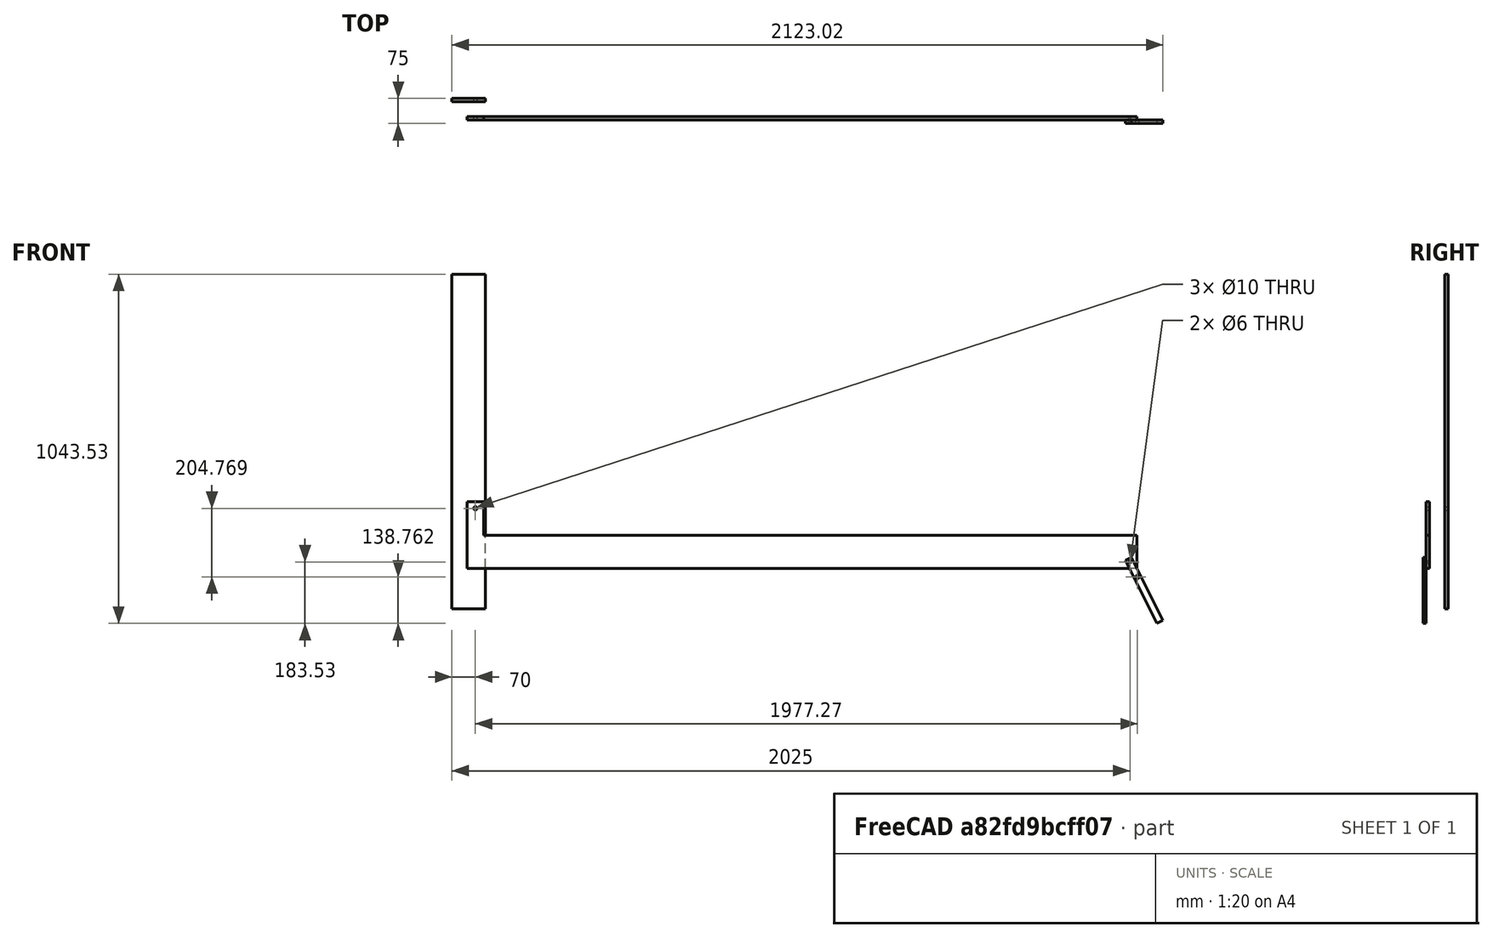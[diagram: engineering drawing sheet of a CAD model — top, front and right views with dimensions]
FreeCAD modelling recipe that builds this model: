
FCSTD DOCUMENT  (FreeCAD 2022.524R14555 (Git shallow))
Label: assembly
License: All rights reserved
LicenseURL: http://en.wikipedia.org/wiki/All_rights_reserved
objects: Part::FeaturePython×17, App::FeaturePython×13, Sketcher::SketchObject×5, PartDesign::Body×4, PartDesign::Pad×3, PartDesign::Hole×3, Part::SubShapeBinder×2, PartDesign::SubShapeBinder×1
note: 46 computed .brp shape members not serialized (recipe doc carries the construction recipe); baked Part::Feature solids carry a one-line shape summary decoded from their .brp

FEATURE [Sketcher::SketchObject] Sketch
  FullyConstrained = true
  MapMode = 5
  Placement = pos=(0,0,0) rot=(1,0,0;1.5708rad)
  Support = -> [XZ_Plane]
  TreeRank = 27
  sketch-geometry (5):
    g0: LineSegment StartX=0 StartY=0 StartZ=0 EndX=100 EndY=0 EndZ=0
    g1: LineSegment StartX=100 StartY=0 StartZ=0 EndX=100 EndY=1000 EndZ=0
    g2: LineSegment StartX=100 StartY=1000 StartZ=0 EndX=0 EndY=1000 EndZ=0
    g3: LineSegment StartX=0 StartY=1000 StartZ=0 EndX=0 EndY=0 EndZ=0
    g4: Circle CenterX=70 CenterY=300 CenterZ=0 NormalX=0 NormalY=0 NormalZ=1 AngleXU=0 Radius=5
  constraints (14):
    c: Coincident(g0,g1)
    c: Coincident(g1,g2)
    c: Coincident(g2,g3)
    c: Coincident(g3,g0)
    c: Horizontal(g0)
    c: Horizontal(g2)
    c: Vertical(g1)
    c: Vertical(g3)
    c: Coincident(g0,g-1)
    c: Distance(g0) = 100
    c: Distance(g1) = 1000
    c: Diameter(g4) = 10
    c: DistanceY(g0,g4) = 300
    c: DistanceX(g4,g0) = 30
FEATURE [PartDesign::Pad] Pad
  AddSubType = 0
  AlongSketchNormal = false
  CheckUpToFaceLimits = true
  ClaimChildren = false
  Direction = (0,-1,2e-16)
  Fit = 0
  FitJoin = 0
  InnerFit = 0
  InnerFitJoin = 0
  InnerTaperAngle = 0
  InnerTaperAngleRev = 0
  Length = 10
  Length2 = 100
  Linearize = true
  NewSolid = false
  Placement = pos=(0,0,0) rot=(1,0,0;1.5708rad)
  Profile = -> Sketch
  Suppress = false
  TreeRank = 28
  Type = 0
  _ProfileBasedVersion = 1
FEATURE [Sketcher::SketchObject] Sketch001
  FullyConstrained = false
  MapMode = 5
  Placement = pos=(1.13238e+06,-2.32641e+06,1.04291e+07) rot=(0.99859,0.005814,-0.052765;3.36076rad)
  TreeRank = 42
  sketch-geometry (7):
    g0: LineSegment StartX=2173.24 StartY=237.393 StartZ=0 EndX=2173.24 EndY=137.393 EndZ=0
    g1: LineSegment StartX=2173.24 StartY=137.393 StartZ=0 EndX=173.238 EndY=137.393 EndZ=0
    g2: LineSegment StartX=173.238 StartY=137.393 StartZ=0 EndX=173.238 EndY=337.393 EndZ=0
    g3: LineSegment StartX=173.238 StartY=337.393 StartZ=0 EndX=223.238 EndY=337.393 EndZ=0
    g4: LineSegment StartX=223.238 StartY=337.393 StartZ=0 EndX=223.238 EndY=237.393 EndZ=0
    g5: LineSegment StartX=223.238 StartY=237.393 StartZ=0 EndX=2173.24 EndY=237.393 EndZ=0
    g6: Circle CenterX=198.238 CenterY=317.393 CenterZ=0 NormalX=0 NormalY=0 NormalZ=1 AngleXU=0 Radius=5
  constraints (19):
    c: Coincident(g0,g1)
    c: Coincident(g1,g2)
    c: Horizontal(g1)
    c: Vertical(g0)
    c: Vertical(g2)
    c: Coincident(g2,g3)
    c: Horizontal(g3)
    c: Coincident(g3,g4)
    c: Vertical(g4)
    c: Coincident(g4,g5)
    c: Coincident(g5,g0)
    c: Horizontal(g5)
    c: Distance(g1) = 2000
    c: Distance(g0) = 100
    c: Distance(g4) = 100
    c: Distance(g3) = 50
    c: DistanceX(g6,g3) = 25
    c: Diameter(g6) = 10
    c: DistanceY(g6,g2) = 20
FEATURE [PartDesign::Pad] Pad001
  AddSubType = 0
  AlongSketchNormal = false
  CheckUpToFaceLimits = true
  ClaimChildren = false
  Direction = (-0.105384,0.216506,-0.970577)
  Fit = 0
  FitJoin = 0
  InnerFit = 0
  InnerFitJoin = 0
  InnerTaperAngle = 0
  InnerTaperAngleRev = 0
  Length = 10
  Length2 = 100
  Linearize = true
  NewSolid = false
  Placement = pos=(1.13238e+06,-2.32641e+06,1.04291e+07) rot=(0.99859,0.005814,-0.052765;3.36076rad)
  Profile = -> Sketch001
  Suppress = false
  TreeRank = 44
  Type = 0
  _ProfileBasedVersion = 1
FEATURE [Sketcher::SketchObject] Sketch002
  ExternalGeometry = -> [Pad001]
  FullyConstrained = true
  MapMode = 5
  Placement = pos=(1.13238e+06,-2.32641e+06,1.04291e+07) rot=(0.99859,0.005814,-0.052765;3.36076rad)
  Support = -> [Pad001]
  TreeRank = 90
  sketch-geometry (1):
    g0: Circle CenterX=2153.24 CenterY=157.393 CenterZ=0 NormalX=0 NormalY=0 NormalZ=1 AngleXU=0 Radius=5
  constraints (3):
    c: DistanceY(g-3,g0) = 20
    c: DistanceX(g0,g-3) = 20
    c: Diameter(g0) = 10
FEATURE [PartDesign::Hole] Hole
  AddSubType = 1
  BaseFeature = -> Pad001
  ClaimChildren = false
  CustomThreadClearance = 0
  Depth = 25
  DepthType = 0
  Diameter = 6
  DrillForDepth = false
  DrillPoint = 1
  DrillPointAngle = 118
  Fit = 0
  FitJoin = 0
  HoleCutCountersinkAngle = 90
  HoleCutCustomValues = false
  HoleCutDepth = 0
  HoleCutDiameter = 6.1
  HoleCutType = 0
  InnerFit = 0
  InnerFitJoin = 0
  Linearize = true
  ModelThread = false
  NewSolid = false
  Placement = pos=(1.13238e+06,-2.32641e+06,1.04291e+07) rot=(0.99859,0.005814,-0.052765;3.36076rad)
  Profile = -> Sketch002
  Suppress = false
  Tapered = false
  TaperedAngle = 90
  ThreadClass = 0
  ThreadDepth = 23.5
  ThreadDepthType = 0
  ThreadDirection = 0
  ThreadFit = 0
  ThreadSize = 0
  ThreadType = 0
  Threaded = false
  TreeRank = 91
  UseCustomThreadClearance = false
  _ProfileBasedVersion = 1
FEATURE [PartDesign::Body] Body001  label="Ramme"
  AutoGroupSolids = false
  ClaimAllChildren = false
  ExportMode = 0
  Group = -> [Sketch001,Pad001,Sketch002,Hole]
  Origin = -> Origin001
  Placement = pos=(-128.238,-1.07453e+07,-17.3929) rot=(-0.997715,-0.052719,0.042254;1.79251rad)
  Tip = -> Hole
  TreeRank = 41
  _ExportChildren = -> [Pad001,Hole]
  _GroupVersion = 1
FEATURE [Part::SubShapeBinder] Import  label="Import(Hole)"
  BindCopyOnChange = 0
  BindMode = 0
  ClaimChildren = false
  Context = -> Assembly [Parts.Body002.Import.]
  FillStyle = 0
  Fuse = false
  MakeFace = false
  PartialLoad = false
  Relative = true
  Support = -> [Body001[Hole.]]
  TreeRank = 103
  _Version = 8
FEATURE [Sketcher::SketchObject] Sketch003
  ExternalGeometry = -> [Import]
  FullyConstrained = true
  MapMode = 5
  Placement = pos=(8.58341,-49.4299,-44.7434) rot=(0.99755,0.02837,0.063948;2.30829rad)
  Support = -> [Import]
  TreeRank = 102
  sketch-geometry (6):
    g0: LineSegment StartX=1907.59 StartY=351.564 StartZ=0 EndX=1927.59 EndY=351.564 EndZ=0
    g1: LineSegment StartX=1927.59 StartY=351.564 StartZ=0 EndX=1927.59 EndY=141.564 EndZ=0
    g2: LineSegment StartX=1927.59 StartY=141.564 StartZ=0 EndX=1907.59 EndY=141.564 EndZ=0
    g3: LineSegment StartX=1907.59 StartY=141.564 StartZ=0 EndX=1907.59 EndY=351.564 EndZ=0
    g4: Circle CenterX=1917.59 CenterY=341.564 CenterZ=0 NormalX=0 NormalY=0 NormalZ=1 AngleXU=0 Radius=3
    g5: Circle CenterX=1917.59 CenterY=291.564 CenterZ=0 NormalX=0 NormalY=0 NormalZ=1 AngleXU=0 Radius=5
  constraints (17):
    c: Coincident(g0,g1)
    c: Coincident(g1,g2)
    c: Coincident(g2,g3)
    c: Horizontal(g0)
    c: Horizontal(g2)
    c: Vertical(g1)
    c: Vertical(g3)
    c: Coincident(g4,g-3)
    c: Equal(g4,g-3)
    c: DistanceY(g4,g0) = 10
    c: DistanceX(g0,g0) = 20
    c: DistanceX(g4,g0) = 10
    c: Vertical(g5,g4)
    c: DistanceY(g5,g4) = 50
    c: Diameter(g5) = 10
    c: DistanceY(g1,g4) = 200
    c: Coincident(g3,g0)
FEATURE [PartDesign::Pad] Pad002
  AddSubType = 0
  AlongSketchNormal = false
  CheckUpToFaceLimits = true
  ClaimChildren = false
  Direction = (0.127685,-0.73531,-0.665594)
  Fit = 0
  FitJoin = 0
  InnerFit = 0
  InnerFitJoin = 0
  InnerTaperAngle = 0
  InnerTaperAngleRev = 0
  Length = 10
  Length2 = 100
  Linearize = true
  NewSolid = false
  Profile = -> Sketch003
  Suppress = false
  TreeRank = 104
  Type = 0
  _ProfileBasedVersion = 1
FEATURE [Part::SubShapeBinder] Import001  label="Import001(Pad)"
  BindCopyOnChange = 0
  BindMode = 0
  ClaimChildren = false
  Context = -> Assembly [Parts.Body002.Import001.]
  FillStyle = 0
  Fuse = false
  MakeFace = false
  PartialLoad = false
  Relative = true
  Support = -> [Body[Pad.]]
  TreeRank = 110
  _Version = 8
FEATURE [PartDesign::Body] Body002
  AutoGroupSolids = false
  ClaimAllChildren = false
  ExportMode = 0
  Group = -> [Sketch003,Import,Pad002,Import001]
  Origin = -> Origin002
  Placement = pos=(460.15,2.22339,-1019.78) rot=(0.817382,0.464073,0.341354;5.43675rad)
  Tip = -> Pad002
  TreeRank = 101
  _ExportChildren = -> [Import,Pad002,Import001]
  _GroupVersion = 1
FEATURE [PartDesign::SubShapeBinder] Import002  label="Import002(Sketch004)"
  BindCopyOnChange = 0
  BindMode = 0
  ClaimChildren = false
  Context = -> Body003 [Import002.]
  FillStyle = 0
  Fuse = false
  MakeFace = false
  PartialLoad = false
  Relative = true
  Support = -> [Assembly[Parts.Body002.Sketch004.]]
  TreeRank = 122
  _Version = 8
FEATURE [PartDesign::Hole] Hole001
  AddSubType = 1
  ClaimChildren = false
  CustomThreadClearance = 0
  Depth = 25
  DepthType = 0
  Diameter = 6
  DrillForDepth = false
  DrillPoint = 1
  DrillPointAngle = 118
  Fit = 0
  FitJoin = 0
  HoleCutCountersinkAngle = 90
  HoleCutCustomValues = false
  HoleCutDepth = 0
  HoleCutDiameter = 6.1
  HoleCutType = 0
  InnerFit = 0
  InnerFitJoin = 0
  Linearize = true
  ModelThread = false
  NewSolid = false
  Profile = -> Import002 [Edge1]
  Suppress = false
  Tapered = false
  TaperedAngle = 90
  ThreadClass = 0
  ThreadDepth = 23.5
  ThreadDepthType = 0
  ThreadDirection = 0
  ThreadFit = 0
  ThreadSize = 0
  ThreadType = 0
  Threaded = false
  TreeRank = 123
  UseCustomThreadClearance = false
  _ProfileBasedVersion = 1
FEATURE [PartDesign::Body] Body003
  AutoGroupSolids = false
  ClaimAllChildren = false
  ExportMode = 0
  Group = -> [Import002,Hole001]
  Origin = -> Origin003
  Tip = -> Hole001
  TreeRank = 121
  _ExportChildren = -> [Hole001]
  _GroupVersion = 1
FEATURE [Sketcher::SketchObject] Sketch004
  ExternalGeometry = -> [Pad]
  FullyConstrained = true
  MapMode = 5
  Placement = pos=(0,0,0) rot=(1,0,0;1.5708rad)
  Support = -> [XZ_Plane]
  TreeRank = 124
  sketch-geometry (1):
    g0: Circle CenterX=70 CenterY=200 CenterZ=0 NormalX=0 NormalY=0 NormalZ=1 AngleXU=0 Radius=5
  constraints (3):
    c: Diameter(g0) = 10
    c: DistanceX(g-1,g0) = 70
    c: DistanceY(g-1,g0) = 200
FEATURE [PartDesign::Hole] Hole002
  AddSubType = 1
  BaseFeature = -> Pad
  ClaimChildren = false
  CustomThreadClearance = 0
  Depth = 25
  DepthType = 0
  Diameter = 6
  DrillForDepth = false
  DrillPoint = 1
  DrillPointAngle = 118
  Fit = 0
  FitJoin = 0
  HoleCutCountersinkAngle = 90
  HoleCutCustomValues = false
  HoleCutDepth = 0
  HoleCutDiameter = 6.1
  HoleCutType = 0
  InnerFit = 0
  InnerFitJoin = 0
  Linearize = true
  ModelThread = false
  NewSolid = false
  Placement = pos=(0,0,0) rot=(1,0,0;1.5708rad)
  Profile = -> Sketch004
  Suppress = false
  Tapered = false
  TaperedAngle = 90
  ThreadClass = 0
  ThreadDepth = 23.5
  ThreadDepthType = 0
  ThreadDirection = 0
  ThreadFit = 0
  ThreadSize = 0
  ThreadType = 0
  Threaded = false
  TreeRank = 125
  UseCustomThreadClearance = false
  _ProfileBasedVersion = 1
FEATURE [PartDesign::Body] Body  label="Vegg"
  AutoGroupSolids = false
  ClaimAllChildren = false
  ExportMode = 0
  Group = -> [Sketch,Pad,Sketch004,Hole002]
  Origin = -> Origin
  Tip = -> Hole002
  TreeRank = 26
  _ExportChildren = -> [Pad,Hole002]
  _GroupVersion = 1
FEATURE [Part::FeaturePython] Parts  # WARN: FeaturePython — macro-defined, semantics opaque (R4)
  Group = -> [Body,Body001,Body002]
  GroupMode = 0
  TreeRank = 16
  _LinkVersion = 1
FEATURE [Part::FeaturePython] Assembly  # WARN: FeaturePython — macro-defined, semantics opaque (R4)
  AutoRelax = true
  BuildShape = 0
  Freeze = false
  Group = -> [Constraints,Elements,Parts]
  TreeRank = 13
  Verbose = false
  _LinkVersion = 1
  _SolverType = 1
  _Version = 1
FEATURE [App::FeaturePython] Constraints  # WARN: FeaturePython — macro-defined, semantics opaque (R4)
  Group = -> [Constraint,Constraint001,Constraint002,Constraint003]
  TreeRank = 14
  _LinkVersion = 1
  _Version = 1
FEATURE [App::FeaturePython] Elements  # WARN: FeaturePython — macro-defined, semantics opaque (R4)
  Group = -> [_Element,_Element001,_Element002,_Element003,_Element004,_Element005,_Element006,_Element007,_Element008,_Element009,_Element010,_Element011,_Element012,_Element013,_Element014]
  TreeRank = 15
  _LinkVersion = 1
FEATURE [App::FeaturePython] Constraint  label="Locked"  # WARN: FeaturePython — macro-defined, semantics opaque (R4)
  Disabled = true
  Group = -> [ElementLink]
  TreeRank = 29
  _ConstraintType = 0
  _LinkVersion = 1
  _Parent = -> Constraints
FEATURE [App::FeaturePython] ElementLink  label="_Element"  # link proxy (typed FeaturePython)
  LinkTransform = true
  LinkedObject = -> _Element
  TreeRank = 30
  _LinkVersion = 1
  _Parent = -> Constraint
FEATURE [Part::FeaturePython] _Element  # link proxy (typed FeaturePython)
  Detach = false
  LinkTransform = true
  LinkedObject = -> Body [Pad.Face1]
  TreeRank = 31
  _LinkVersion = 1
  _Parent = -> Elements
FEATURE [Part::FeaturePython] _Element001  # link proxy (typed FeaturePython)
  Detach = false
  LinkTransform = true
  LinkedObject = -> Body001 [Pad001.Face7]
  TreeRank = 47
  _LinkVersion = 1
  _Parent = -> Elements
FEATURE [Part::FeaturePython] _Element002  # link proxy (typed FeaturePython)
  Detach = false
  LinkTransform = true
  LinkedObject = -> Body [Pad.Face5]
  TreeRank = 49
  _LinkVersion = 1
  _Parent = -> Elements
FEATURE [Part::FeaturePython] _Element003  # link proxy (typed FeaturePython)
  Detach = false
  LinkTransform = true
  LinkedObject = -> Body001 [Pad001.Vertex9]
  TreeRank = 55
  _LinkVersion = 1
  _Parent = -> Elements
FEATURE [Part::FeaturePython] _Element004  # link proxy (typed FeaturePython)
  Detach = false
  LinkTransform = true
  LinkedObject = -> Body [Pad.Face7]
  TreeRank = 57
  _LinkVersion = 1
  _Parent = -> Elements
FEATURE [Part::FeaturePython] _Element005  # link proxy (typed FeaturePython)
  Detach = false
  LinkTransform = true
  LinkedObject = -> Body001 [Pad001.Vertex7]
  TreeRank = 60
  _LinkVersion = 1
  _Parent = -> Elements
FEATURE [Part::FeaturePython] _Element006  # link proxy (typed FeaturePython)
  Detach = false
  LinkTransform = true
  LinkedObject = -> Body [Pad.Vertex10]
  TreeRank = 67
  _LinkVersion = 1
  _Parent = -> Elements
FEATURE [Part::FeaturePython] _Element007  # link proxy (typed FeaturePython)
  Detach = false
  LinkTransform = true
  LinkedObject = -> Body001 [Pad001.Face8]
  TreeRank = 69
  _LinkVersion = 1
  _Parent = -> Elements
FEATURE [Part::FeaturePython] _Element008  # link proxy (typed FeaturePython)
  Detach = false
  LinkTransform = true
  LinkedObject = -> Body [Pad.Edge15]
  TreeRank = 72
  _LinkVersion = 1
  _Parent = -> Elements
FEATURE [Part::FeaturePython] _Element009  # link proxy (typed FeaturePython)
  Detach = false
  LinkTransform = true
  LinkedObject = -> Body001 [Pad001.Edge20]
  TreeRank = 74
  _LinkVersion = 1
  _Parent = -> Elements
FEATURE [App::FeaturePython] Constraint001  label="AxialAlignment"  # WARN: FeaturePython — macro-defined, semantics opaque (R4)
  Angle = 0
  AnglePitch = 0
  AngleRoll = 0
  Disabled = false
  Group = -> [ElementLink001,ElementLink002]
  LockAngle = false
  Multiply = false
  TreeRank = 75
  _ConstraintType = 36
  _LinkVersion = 1
  _Parent = -> Constraints
FEATURE [App::FeaturePython] ElementLink001  label="_Element001"  # link proxy (typed FeaturePython)
  LinkTransform = true
  LinkedObject = -> _Element001
  TreeRank = 76
  _LinkVersion = 1
  _Parent = -> Constraint001
FEATURE [App::FeaturePython] ElementLink002  label="_Element002"  # link proxy (typed FeaturePython)
  LinkTransform = true
  LinkedObject = -> _Element002
  TreeRank = 77
  _LinkVersion = 1
  _Parent = -> Constraint001
FEATURE [Part::FeaturePython] _Element010  # link proxy (typed FeaturePython)
  Detach = false
  LinkTransform = true
  LinkedObject = -> Body001 [Pad001.Vertex8]
  TreeRank = 80
  _LinkVersion = 1
  _Parent = -> Elements
FEATURE [Part::FeaturePython] _Element011  # WARN: FeaturePython — macro-defined, semantics opaque (R4)
  Detach = false
  LinkTransform = true
  TreeRank = 85
  _LinkVersion = 1
  _Parent = -> Elements
FEATURE [App::FeaturePython] Constraint002  label="SameOrientation"  # WARN: FeaturePython — macro-defined, semantics opaque (R4)
  Disabled = true
  Group = -> [ElementLink003,ElementLink004]
  TreeRank = 86
  _ConstraintType = 2
  _LinkVersion = 1
  _Parent = -> Constraints
FEATURE [App::FeaturePython] ElementLink003  label="_Element"  # link proxy (typed FeaturePython)
  LinkTransform = true
  LinkedObject = -> _Element
  TreeRank = 87
  _LinkVersion = 1
  _Parent = -> Constraint002
FEATURE [App::FeaturePython] ElementLink004  label="_Element012"  # link proxy (typed FeaturePython)
  LinkTransform = true
  LinkedObject = -> _Element012
  TreeRank = 88
  _LinkVersion = 1
  _Parent = -> Constraint002
FEATURE [Part::FeaturePython] _Element012  # link proxy (typed FeaturePython)
  Detach = false
  LinkTransform = true
  LinkedObject = -> Body001 [Pad001.Face2]
  TreeRank = 89
  _LinkVersion = 1
  _Parent = -> Elements
FEATURE [App::FeaturePython] Constraint003  label="AxialAlignment001"  # WARN: FeaturePython — macro-defined, semantics opaque (R4)
  Angle = 0
  AnglePitch = 0
  AngleRoll = 0
  Disabled = false
  Group = -> [ElementLink005,ElementLink006]
  LockAngle = false
  Multiply = false
  TreeRank = 105
  _ConstraintType = 36
  _LinkVersion = 1
  _Parent = -> Constraints
FEATURE [App::FeaturePython] ElementLink005  label="_Element013"  # link proxy (typed FeaturePython)
  LinkTransform = true
  LinkedObject = -> _Element013
  TreeRank = 106
  _LinkVersion = 1
  _Parent = -> Constraint003
FEATURE [Part::FeaturePython] _Element013  # link proxy (typed FeaturePython)
  Detach = false
  LinkTransform = true
  LinkedObject = -> Body002 [Pad002.Face6]
  TreeRank = 107
  _LinkVersion = 1
  _Parent = -> Elements
FEATURE [App::FeaturePython] ElementLink006  label="_Element014"  # link proxy (typed FeaturePython)
  LinkTransform = true
  LinkedObject = -> _Element014
  TreeRank = 108
  _LinkVersion = 1
  _Parent = -> Constraint003
FEATURE [Part::FeaturePython] _Element014  # link proxy (typed FeaturePython)
  Detach = false
  LinkTransform = true
  LinkedObject = -> Body001 [Hole.Face9]
  TreeRank = 109
  _LinkVersion = 1
  _Parent = -> Elements
